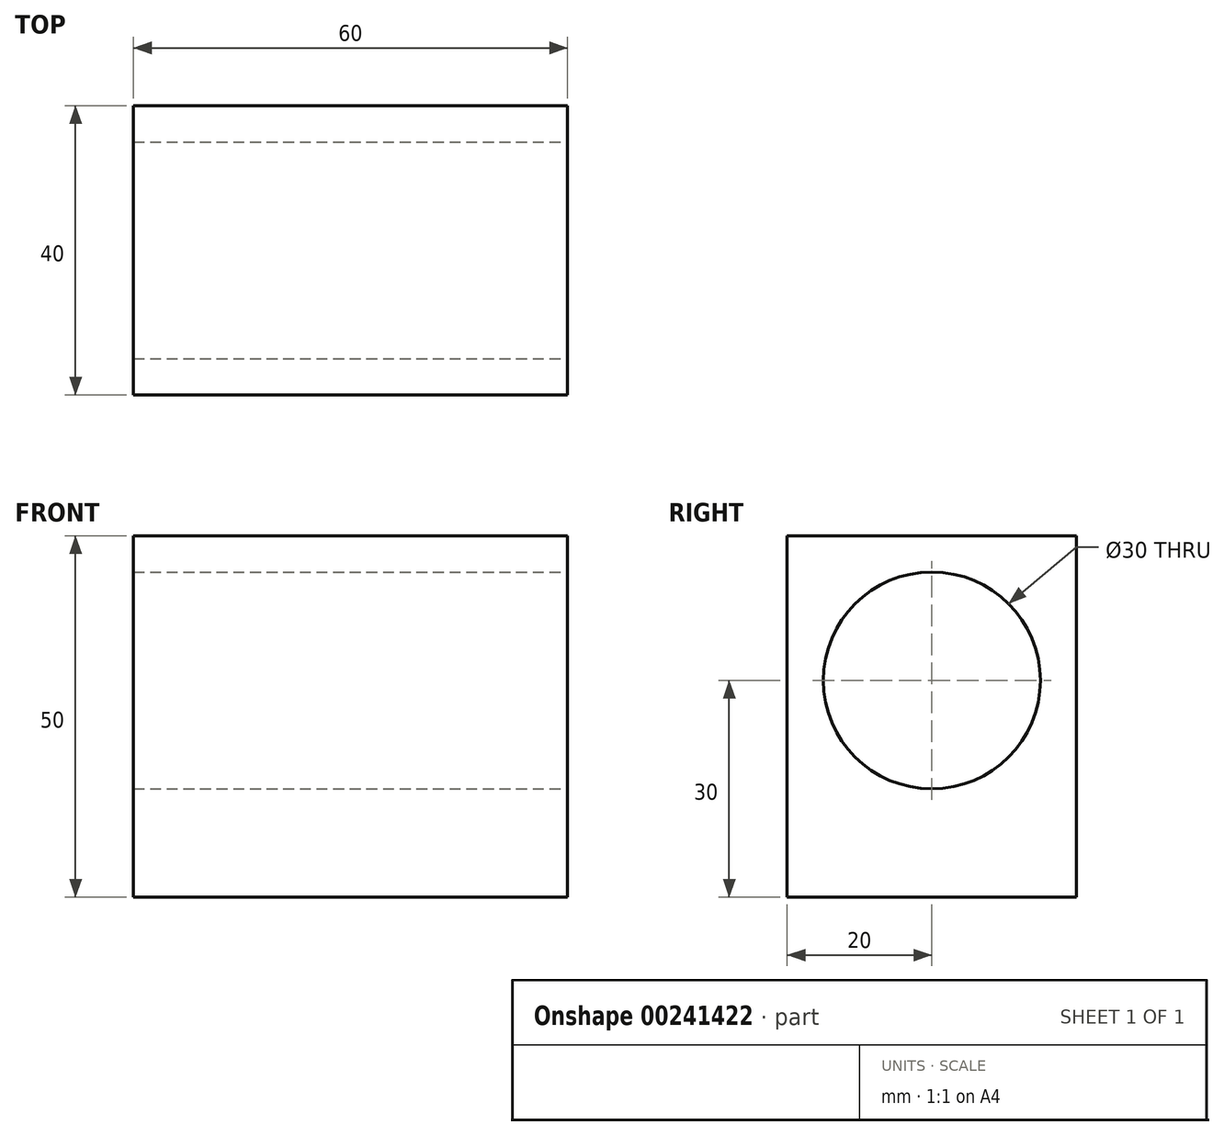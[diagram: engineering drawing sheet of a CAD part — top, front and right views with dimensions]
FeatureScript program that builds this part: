
annotation { "Feature Type Name" : "Feature", "Feature Type Description" : "" }
export const myFeature = defineFeature(function(context is Context, id is Id, definition is map)
    precondition{}
    {
        {
            var Q0;
            Q0=qCreatedBy(makeId("Top.planeOp"),FACE);
            var sketch = newSketch(context, id + "F0", { "sketchPlane" : qUnion([Q0])});
            skLineSegment(sketch, "E0.bottom", {"start": v(-30, 20) * mm, "end": v(30, 20) * mm});
            skLineSegment(sketch, "E0.top", {"start": v(-30, -20) * mm, "end": v(30, -20) * mm});
            skLineSegment(sketch, "E0.left", {"start": v(-30, 20) * mm, "end": v(-30, -20) * mm});
            skLineSegment(sketch, "E0.right", {"start": v(30, 20) * mm, "end": v(30, -20) * mm});
            skPoint(sketch, "E0.middle", {"position": v(0, 0) * mm});
            skSolve(sketch);
        }
        {
            var Q0;
            Q0=makeQuery(id+"F0.imprint","IMPRINT",FACE,{"disambiguationData":[TD([[makeQuery(id+"F0.imprint","IMPRINT",EDGE,{"derivedFrom":sQuery(id+"F0.wireOp",EDGE,"E0.bottom")}),-1.0]])]});
            extrude(context, id + "F1", {"entities" : qUnion([Q0]), "depth" : 50 * mm});
        }
        {
            var Q0;
            Q0=makeQuery(id+"F1.opExtrude","SWEPT_FACE",FACE,{"disambiguationData":[OSD([sQuery(id+"F0.wireOp",EDGE,"E0.right")])]});
            var sketch = newSketch(context, id + "F2", { "sketchPlane" : qUnion([Q0])});
            skCircle(sketch, "E1", {"center": v(0, 30) * mm, "radius": 15 * mm});
            skSolve(sketch);
        }
        {
            var Q0;
            Q0 = qSketchRegion(id + "F2", true);
            extrude(context, id + "F3", {"entities" : qUnion([Q0]), "operationType" : NewBodyOperationType.REMOVE, "endBound" : BoundingType.THROUGH_ALL, "oppositeDirection" : true, "depth" : 25 * mm});
        }
    });
